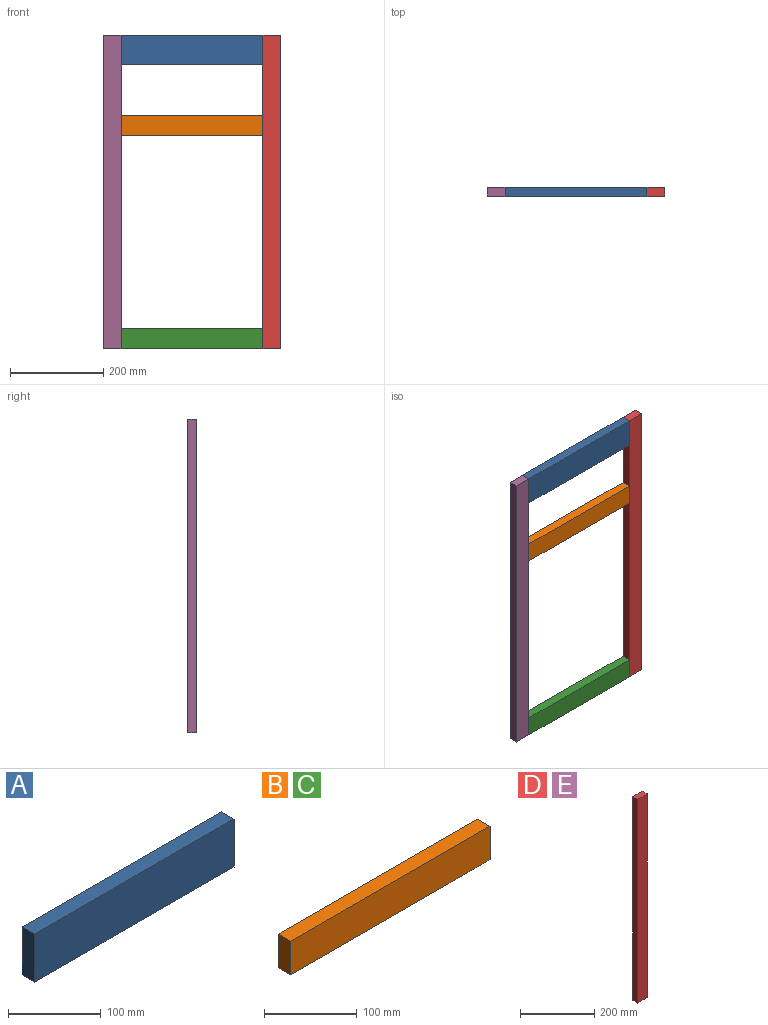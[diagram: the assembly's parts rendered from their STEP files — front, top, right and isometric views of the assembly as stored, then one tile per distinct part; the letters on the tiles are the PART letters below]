
ASSEMBLY  parts=5 mates=4
PART A: 6 faces, bbox 304.8x19.1x63.5 mm
  f0: plane 304.8x19.05mm, normal (0,0,1), area 5806.4mm2, adj f1,f3,f4,f5
  f1: plane 63.5x19.05mm, normal (-1,0,0), area 1209.7mm2, adj f0,f2,f4,f5
  f2: plane 304.8x19.05mm, normal (0,0,-1), area 5806.4mm2, adj f1,f3,f4,f5
  f3: plane 63.5x19.05mm, normal (1,0,0), area 1209.7mm2, adj f0,f2,f4,f5
  f4: plane 304.8x63.5mm, normal (0,-1,0), area 19354.8mm2, adj f0,f1,f2,f3
  f5: plane 304.8x63.5mm, normal (0,1,0), area 19354.8mm2, adj f0,f1,f2,f3
PART B: 6 faces, bbox 304.8x19.1x44.5 mm
  f0: plane 304.8x19.05mm, normal (0,0,1), area 5806.4mm2, adj f1,f3,f4,f5
  f1: plane 44.45x19.05mm, normal (-1,0,0), area 846.8mm2, adj f0,f2,f4,f5
  f2: plane 304.8x19.05mm, normal (0,0,-1), area 5806.4mm2, adj f1,f3,f4,f5
  f3: plane 44.45x19.05mm, normal (1,0,0), area 846.8mm2, adj f0,f2,f4,f5
  f4: plane 304.8x44.45mm, normal (0,-1,0), area 13548.4mm2, adj f0,f1,f2,f3
  f5: plane 304.8x44.45mm, normal (0,1,0), area 13548.4mm2, adj f0,f1,f2,f3
PART C: same geometry as B
PART D: 6 faces, bbox 38.1x19.1x673.1 mm
  f0: plane 38.1x19.05mm, normal (0,0,1), area 725.8mm2, adj f1,f3,f4,f5
  f1: plane 673.1x19.05mm, normal (-1,0,0), area 12822.6mm2, adj f0,f2,f4,f5
  f2: plane 38.1x19.05mm, normal (0,0,-1), area 725.8mm2, adj f1,f3,f4,f5
  f3: plane 673.1x19.05mm, normal (1,0,0), area 12822.6mm2, adj f0,f2,f4,f5
  f4: plane 673.1x38.1mm, normal (0,-1,0), area 25645.1mm2, adj f0,f1,f2,f3
  f5: plane 673.1x38.1mm, normal (0,1,0), area 25645.1mm2, adj f0,f1,f2,f3
PART E: same geometry as D
PLACE A t=(-52.26,-217.69,-216.29)mm
PLACE B t=(-52.26,-217.69,-368.69)mm
PLACE C t=(-52.26,-217.69,-825.89)mm
PLACE D t=(-14.16,-217.69,-825.89)mm
PLACE E t=(-357.06,-217.69,-825.89)mm
MATE fastened D.f4 <-> C.f4  axis (0,-1,0) through (-52.26,-236.74,-825.89)mm
MATE fastened E.f4 <-> A.f4  axis (0,-1,0) through (-357.06,-236.74,-152.79)mm
MATE fastened A.f4 <-> B.f4  axis (0,-1,0) through (-52.26,-236.74,-216.29)mm
MATE fastened A.f4 <-> D.f4  axis (0,-1,0) through (-52.26,-236.74,-152.79)mm
